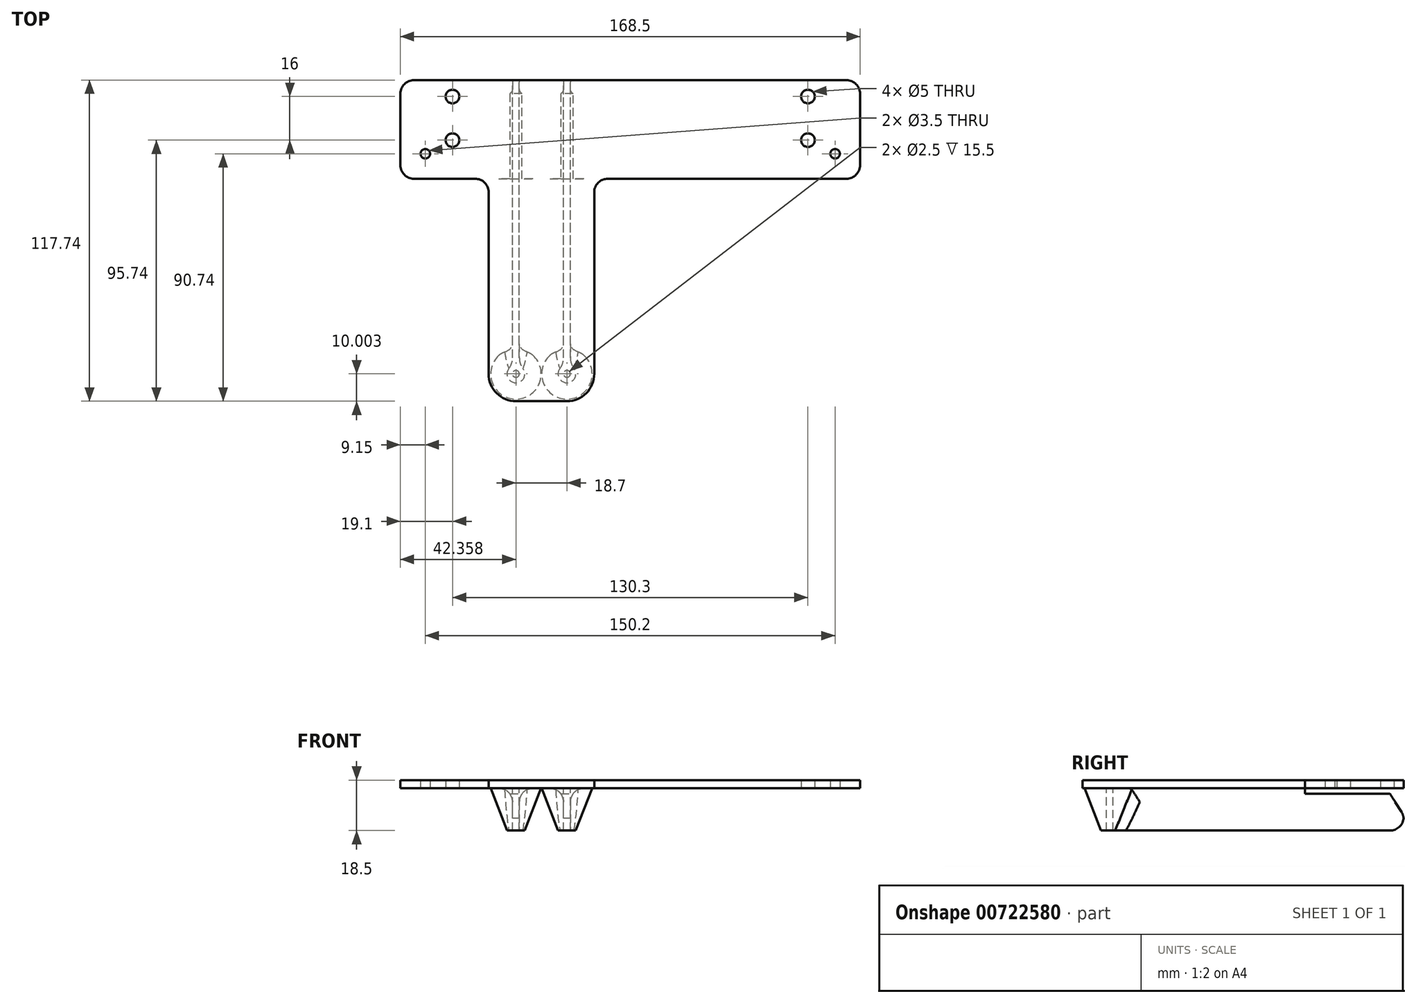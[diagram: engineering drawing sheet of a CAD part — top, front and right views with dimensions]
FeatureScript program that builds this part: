
annotation { "Feature Type Name" : "Feature", "Feature Type Description" : "" }
export const myFeature = defineFeature(function(context is Context, id is Id, definition is map)
    precondition{}
    {
        {
            var Q0;
            Q0=qCreatedBy(makeId("Top.planeOp"),FACE);
            var sketch = newSketch(context, id + "F0", { "sketchPlane" : qUnion([Q0])});
            skLineSegment(sketch, "E0", {"start": v(0, 0) * mm, "end": v(75.1, 0) * mm, "construction": true});
            skCircle(sketch, "E1", {"center": v(75.1, 0) * mm, "radius": 1.75 * mm});
            skCircle(sketch, "E2", {"center": v(75.1, 0) * mm, "radius": 4.15 * mm, "construction": true});
            skLineSegment(sketch, "E3", {"start": v(0, 0) * mm, "end": v(0, 27) * mm, "construction": true});
            skLineSegment(sketch, "E4", {"start": v(0, 5) * mm, "end": v(65.15, 5) * mm, "construction": true});
            skLineSegment(sketch, "E5", {"start": v(65.15, 5) * mm, "end": v(65.15, 21) * mm, "construction": true});
            skCircle(sketch, "E6", {"center": v(65.15, 5) * mm, "radius": 2.5 * mm});
            skCircle(sketch, "E7", {"center": v(65.15, 21) * mm, "radius": 2.5 * mm});
            skCircle(sketch, "E8", {"center": v(-41.9, -80.74) * mm, "radius": 3.25 * mm});
            skCircle(sketch, "E9", {"center": v(-23.2, -80.74) * mm, "radius": 3.25 * mm});
            skCircle(sketch, "E10", {"center": v(-65.15, 5) * mm, "radius": 2.5 * mm});
            skCircle(sketch, "E11", {"center": v(-65.15, 21) * mm, "radius": 2.5 * mm});
            skLineSegment(sketch, "E12", {"start": v(-65.15, 5) * mm, "end": v(0, 5) * mm, "construction": true});
            skCircle(sketch, "E13", {"center": v(-75.1, 0) * mm, "radius": 1.75 * mm});
            skCircle(sketch, "E14", {"center": v(-75.1, 0) * mm, "radius": 4.15 * mm, "construction": true});
            skLineSegment(sketch, "E15", {"start": v(-75.1, 0) * mm, "end": v(0, 0) * mm, "construction": true});
            skLineSegment(sketch, "E16.bottom", {"start": v(-84.25, 27) * mm, "end": v(84.25, 27) * mm});
            skLineSegment(sketch, "E16.top", {"start": v(-84.25, -9.15) * mm, "end": v(84.25, -9.15) * mm});
            skLineSegment(sketch, "E16.left", {"start": v(-84.25, 27) * mm, "end": v(-84.25, -9.15) * mm});
            skLineSegment(sketch, "E16.right", {"start": v(84.25, 27) * mm, "end": v(84.25, -9.15) * mm});
            skArc(sketch, "E17", {"start": v(-51.9, -80.74) * mm, "mid": v(-48.96, -87.8) * mm, "end": v(-41.9, -90.74) * mm});
            skArc(sketch, "E18", {"start": v(-13.2, -80.74) * mm, "mid": v(-16.12, -87.8) * mm, "end": v(-23.2, -90.74) * mm});
            skLineSegment(sketch, "E19", {"start": v(-41.9, -90.74) * mm, "end": v(-23.2, -90.74) * mm});
            skLineSegment(sketch, "E20", {"start": v(-13.2, -80.74) * mm, "end": v(-13.2, -9.15) * mm});
            skLineSegment(sketch, "E21", {"start": v(-51.9, -80.74) * mm, "end": v(-51.9, -9.15) * mm});
            skCircle(sketch, "E22", {"center": v(-23.2, -80.74) * mm, "radius": 1.25 * mm});
            skCircle(sketch, "E23", {"center": v(-41.9, -80.74) * mm, "radius": 1.25 * mm});
            skLineSegment(sketch, "E24", {"start": v(-43.14, -80.74) * mm, "end": v(-43.14, -9.15) * mm});
            skLineSegment(sketch, "E25", {"start": v(-40.64, -80.74) * mm, "end": v(-40.64, -9.15) * mm});
            skLineSegment(sketch, "E26", {"start": v(-24.44, -80.74) * mm, "end": v(-24.44, -9.15) * mm});
            skLineSegment(sketch, "E27", {"start": v(-21.94, -80.74) * mm, "end": v(-21.94, -9.15) * mm});
            skLineSegment(sketch, "E28", {"start": v(-43.14, -9.15) * mm, "end": v(-43.14, 27) * mm});
            skLineSegment(sketch, "E29", {"start": v(-40.64, -9.15) * mm, "end": v(-40.64, 27) * mm});
            skLineSegment(sketch, "E30", {"start": v(-24.44, -9.15) * mm, "end": v(-24.44, 27) * mm});
            skLineSegment(sketch, "E31", {"start": v(-21.94, -9.15) * mm, "end": v(-21.94, 27) * mm});
            skSolve(sketch);
        }
        {
            var Q0;
            Q0=makeQuery(id+"F0.imprint","IMPRINT",FACE,{"disambiguationData":[TD([[makeQuery(id+"F0.imprint","IMPRINT",EDGE,{"derivedFrom":sQuery(id+"F0.wireOp",EDGE,"E8")}),-1.0]])]});
            var Q1;
            Q1=makeQuery(id+"F0.imprint","IMPRINT",FACE,{"disambiguationData":[TD([[makeQuery(id+"F0.imprint","IMPRINT",EDGE,{"derivedFrom":sQuery(id+"F0.wireOp",EDGE,"E8")}),1.0]])]});
            var Q2;
            Q2=makeQuery(id+"F0.imprint","IMPRINT",FACE,{"disambiguationData":[TD([[makeQuery(id+"F0.imprint","IMPRINT",EDGE,{"derivedFrom":sQuery(id+"F0.wireOp",EDGE,"E23")}),1.0]])]});
            var Q3;
            Q3=makeQuery(id+"F0.imprint","IMPRINT",FACE,{"disambiguationData":[TD([[makeQuery(id+"F0.imprint","IMPRINT",EDGE,{"derivedFrom":sQuery(id+"F0.wireOp",EDGE,"E9")}),1.0]])]});
            var Q4;
            Q4=makeQuery(id+"F0.imprint","IMPRINT",FACE,{"disambiguationData":[TD([[makeQuery(id+"F0.imprint","IMPRINT",EDGE,{"derivedFrom":sQuery(id+"F0.wireOp",EDGE,"E22")}),1.0]])]});
            var Q5;
            Q5=makeQuery(id+"F0.imprint","IMPRINT",FACE,{"disambiguationData":[TD([[makeQuery(id+"F0.imprint","IMPRINT",EDGE,{"derivedFrom":sQuery(id+"F0.wireOp",EDGE,"E1")}),-1.0]])]});
            var Q6;
            Q6=makeQuery(id+"F0.imprint","IMPRINT",FACE,{"disambiguationData":[TD([[makeQuery(id+"F0.imprint","IMPRINT",EDGE,{"derivedFrom":sQuery(id+"F0.wireOp",EDGE,"E17")}),1.0]])]});
            var Q7;
            {var subQ0=sQuery(id+"F0.wireOp",EDGE,"E26");var subQ1=sQuery(id+"F0.wireOp",EDGE,"E9");var subQ2=makeQuery(id+"F0.imprint","INTERSECT",VERTEX,{"derivedFrom":[subQ1,subQ0]});Q7=makeQuery(id+"F0.imprint","IMPRINT",FACE,{"disambiguationData":[TD([[makeQuery(id+"F0.imprint","IMPRINT",EDGE,{"disambiguationData":[TD([[subQ2,1.0]])],"derivedFrom":subQ1}),-1.0]])]});}
            var Q8;
            {var subQ0=sQuery(id+"F0.wireOp",EDGE,"E30");Q8=makeQuery(id+"F0.imprint","IMPRINT",FACE,{"disambiguationData":[TD([[makeQuery(id+"F0.imprint","IMPRINT",EDGE,{"derivedFrom":subQ0}),-1.0]])]});}
            var Q9;
            {var subQ0=sQuery(id+"F0.wireOp",EDGE,"E29");Q9=makeQuery(id+"F0.imprint","IMPRINT",FACE,{"disambiguationData":[TD([[makeQuery(id+"F0.imprint","IMPRINT",EDGE,{"derivedFrom":subQ0}),-1.0]])]});}
            var Q10;
            {var subQ0=sQuery(id+"F0.wireOp",EDGE,"E28");Q10=makeQuery(id+"F0.imprint","IMPRINT",FACE,{"disambiguationData":[TD([[makeQuery(id+"F0.imprint","IMPRINT",EDGE,{"derivedFrom":subQ0}),-1.0]])]});}
            var Q11;
            Q11=makeQuery(id+"F0.imprint","IMPRINT",FACE,{"disambiguationData":[TD([[makeQuery(id+"F0.imprint","IMPRINT",EDGE,{"derivedFrom":sQuery(id+"F0.wireOp",EDGE,"E10")}),-1.0]])]});
            extrude(context, id + "F1", {"entities" : qUnion([Q0, Q1, Q2, Q3, Q4, Q5, Q6, Q7, Q8, Q9, Q10, Q11]), "depth" : 3 * mm, "offsetDistance" : 25 * mm});
        }
        {
            var Q0;
            Q0=makeQuery(id+"F0.imprint","IMPRINT",FACE,{"disambiguationData":[TD([[makeQuery(id+"F0.imprint","IMPRINT",EDGE,{"derivedFrom":sQuery(id+"F0.wireOp",EDGE,"E8")}),1.0]])]});
            var Q1;
            Q1=makeQuery(id+"F0.imprint","IMPRINT",FACE,{"disambiguationData":[TD([[makeQuery(id+"F0.imprint","IMPRINT",EDGE,{"derivedFrom":sQuery(id+"F0.wireOp",EDGE,"E9")}),1.0]])]});
            var Q2;
            {var subQ0=sQuery(id+"F0.wireOp",EDGE,"E26");var subQ1=sQuery(id+"F0.wireOp",EDGE,"E9");var subQ2=makeQuery(id+"F0.imprint","INTERSECT",VERTEX,{"derivedFrom":[subQ1,subQ0]});Q2=makeQuery(id+"F0.imprint","IMPRINT",FACE,{"disambiguationData":[TD([[makeQuery(id+"F0.imprint","IMPRINT",EDGE,{"disambiguationData":[TD([[subQ2,1.0]])],"derivedFrom":subQ1}),-1.0]])]});}
            var Q3;
            {var subQ0=sQuery(id+"F0.wireOp",EDGE,"E24");var subQ1=sQuery(id+"F0.wireOp",EDGE,"E8");var subQ2=makeQuery(id+"F0.imprint","INTERSECT",VERTEX,{"derivedFrom":[subQ1,subQ0]});Q3=makeQuery(id+"F0.imprint","IMPRINT",FACE,{"disambiguationData":[TD([[makeQuery(id+"F0.imprint","IMPRINT",EDGE,{"disambiguationData":[TD([[subQ2,1.0]])],"derivedFrom":subQ1}),-1.0]])]});}
            var Q4;
            {var subQ0=sQuery(id+"F0.wireOp",EDGE,"E30");Q4=makeQuery(id+"F0.imprint","IMPRINT",FACE,{"disambiguationData":[TD([[makeQuery(id+"F0.imprint","IMPRINT",EDGE,{"derivedFrom":subQ0}),-1.0]])]});}
            var Q5;
            {var subQ0=sQuery(id+"F0.wireOp",EDGE,"E28");Q5=makeQuery(id+"F0.imprint","IMPRINT",FACE,{"disambiguationData":[TD([[makeQuery(id+"F0.imprint","IMPRINT",EDGE,{"derivedFrom":subQ0}),-1.0]])]});}
            extrude(context, id + "F2", {"entities" : qUnion([Q0, Q1, Q2, Q3, Q4, Q5]), "operationType" : NewBodyOperationType.ADD, "oppositeDirection" : true, "depth" : 15.5 * mm, "offsetDistance" : 25 * mm});
        }
        {
            var Q0;
            {var subQ0=sQuery(id+"F0.wireOp",EDGE,"E30");Q0=makeQuery(id+"F0.imprint","IMPRINT",FACE,{"disambiguationData":[TD([[makeQuery(id+"F0.imprint","IMPRINT",EDGE,{"derivedFrom":subQ0}),-1.0]])]});}
            var Q1;
            {var subQ0=sQuery(id+"F0.wireOp",EDGE,"E28");Q1=makeQuery(id+"F0.imprint","IMPRINT",FACE,{"disambiguationData":[TD([[makeQuery(id+"F0.imprint","IMPRINT",EDGE,{"derivedFrom":subQ0}),-1.0]])]});}
            extrude(context, id + "F3", {"entities" : qUnion([Q0, Q1]), "operationType" : NewBodyOperationType.REMOVE, "oppositeDirection" : true, "depth" : 2 * mm, "offsetDistance" : 25 * mm});
        }
        {
            var Q0;
            Q0=makeQuery(id+"F2.opExtrude","CAP_EDGE",EDGE,{"disambiguationData":[OSD([sQuery(id+"F0.wireOp",EDGE,"E9")])],"isStart":true});
            var Q1;
            Q1=makeQuery(id+"F2.opExtrude","CAP_EDGE",EDGE,{"disambiguationData":[OSD([sQuery(id+"F0.wireOp",EDGE,"E8")])],"isStart":true});
            chamfer(context, id + "F4", {"entities" : qUnion([Q0, Q1]), "chamferType" : ChamferType.TWO_OFFSETS, "width1" : 6 * mm, "oppositeDirection" : false, "width2" : 15.5 * mm, "tangentPropagation" : true});
        }
        {
            var Q0;
            {var subQ0=sQuery(id+"F0.wireOp",EDGE,"E16.bottom");Q0=makeQuery(id+"F3.boolean.opBoolean","COPY",EDGE,{"derivedFrom":makeQuery(id+"F3.opExtrude","CAP_EDGE",EDGE,{"disambiguationData":[OSD([subQ0]),TDD([makeQuery(id+"F0.imprint","IMPRINT",EDGE,{"disambiguationData":[TD([[makeQuery(id+"F0.imprint","INTERSECT",VERTEX,{"derivedFrom":[subQ0,sQuery(id+"F0.wireOp",EDGE,"E30")]}),-1.0]])],"derivedFrom":subQ0})])],"isStart":false})});}
            var Q1;
            {var subQ0=sQuery(id+"F0.wireOp",EDGE,"E16.bottom");Q1=makeQuery(id+"F3.boolean.opBoolean","COPY",EDGE,{"derivedFrom":makeQuery(id+"F3.opExtrude","CAP_EDGE",EDGE,{"disambiguationData":[OSD([subQ0]),TDD([makeQuery(id+"F0.imprint","IMPRINT",EDGE,{"disambiguationData":[TD([[makeQuery(id+"F0.imprint","INTERSECT",VERTEX,{"derivedFrom":[subQ0,sQuery(id+"F0.wireOp",EDGE,"E28")]}),-1.0]])],"derivedFrom":subQ0})])],"isStart":false})});}
            chamfer(context, id + "F5", {"entities" : qUnion([Q0, Q1]), "chamferType" : ChamferType.TWO_OFFSETS, "width1" : 8 * mm, "oppositeDirection" : false, "width2" : 5 * mm, "tangentPropagation" : true});
        }
        {
            var Q0;
            Q0=makeQuery(id+"F1.opExtrude","SWEPT_EDGE",EDGE,{"disambiguationData":[OSD([sQuery(id+"F0.wireOp",EDGE,"E16.top"),sQuery(id+"F0.wireOp",EDGE,"E16.right")])]});
            var Q1;
            Q1=makeQuery(id+"F1.opExtrude","SWEPT_EDGE",EDGE,{"disambiguationData":[OSD([sQuery(id+"F0.wireOp",EDGE,"E16.bottom"),sQuery(id+"F0.wireOp",EDGE,"E16.right")])]});
            var Q2;
            Q2=makeQuery(id+"F1.opExtrude","SWEPT_EDGE",EDGE,{"disambiguationData":[OSD([sQuery(id+"F0.wireOp",EDGE,"E16.top"),sQuery(id+"F0.wireOp",EDGE,"E16.left")])]});
            var Q3;
            Q3=makeQuery(id+"F1.opExtrude","SWEPT_EDGE",EDGE,{"disambiguationData":[OSD([sQuery(id+"F0.wireOp",EDGE,"E16.bottom"),sQuery(id+"F0.wireOp",EDGE,"E16.left")])]});
            var Q4;
            Q4=makeQuery(id+"F1.opExtrude","SWEPT_EDGE",EDGE,{"disambiguationData":[OSD([sQuery(id+"F0.wireOp",EDGE,"E16.top"),sQuery(id+"F0.wireOp",EDGE,"E21")])]});
            var Q5;
            Q5=makeQuery(id+"F1.opExtrude","SWEPT_EDGE",EDGE,{"disambiguationData":[OSD([sQuery(id+"F0.wireOp",EDGE,"E16.top"),sQuery(id+"F0.wireOp",EDGE,"E20")])]});
            var Q6;
            {var subQ0=sQuery(id+"F0.wireOp",EDGE,"E16.bottom");Q6=makeQuery(id+"F2.opExtrude","CAP_EDGE",EDGE,{"disambiguationData":[OSD([subQ0]),TDD([makeQuery(id+"F0.imprint","IMPRINT",EDGE,{"disambiguationData":[TD([[makeQuery(id+"F0.imprint","INTERSECT",VERTEX,{"derivedFrom":[subQ0,sQuery(id+"F0.wireOp",EDGE,"E30")]}),-1.0]])],"derivedFrom":subQ0})])],"isStart":false});}
            var Q7;
            {var subQ0=sQuery(id+"F0.wireOp",EDGE,"E16.bottom");Q7=makeQuery(id+"F2.opExtrude","CAP_EDGE",EDGE,{"disambiguationData":[OSD([subQ0]),TDD([makeQuery(id+"F0.imprint","IMPRINT",EDGE,{"disambiguationData":[TD([[makeQuery(id+"F0.imprint","INTERSECT",VERTEX,{"derivedFrom":[subQ0,sQuery(id+"F0.wireOp",EDGE,"E28")]}),-1.0]])],"derivedFrom":subQ0})])],"isStart":false});}
            var Q8;
            {var subQ1=sQuery(id+"F0.wireOp",EDGE,"E30");var subQ3=sQuery(id+"F0.wireOp",EDGE,"E26");var subQ4=sQuery(id+"F0.wireOp",EDGE,"E16.bottom");var subQ5=makeQuery(id+"F0.imprint","IMPRINT",EDGE,{"disambiguationData":[TD([[makeQuery(id+"F0.imprint","INTERSECT",VERTEX,{"derivedFrom":[subQ4,subQ1]}),-1.0]])],"derivedFrom":subQ4});Q8=makeQuery(id+"F5.opChamfer","BLEND_EDGE",EDGE,{"blendedFrom":[makeQuery(id+"F3.boolean.opBoolean","COPY",EDGE,{"derivedFrom":makeQuery(id+"F3.opExtrude","CAP_EDGE",EDGE,{"disambiguationData":[OSD([subQ4]),TDD([subQ5])],"isStart":false})}),makeQuery(id+"F3.boolean.opBoolean","SPLIT",FACE,{"disambiguationData":[TD([makeQuery(id+"F2.opExtrude","SWEPT_FACE",FACE,{"disambiguationData":[OSD([subQ3,subQ1])]})])],"derivedFrom":makeQuery(id+"F2.boolean.opBoolean","MERGE",FACE,{"derivedFrom":[makeQuery(id+"F1.opExtrude","SWEPT_FACE",FACE,{"disambiguationData":[OSD([subQ4])]}),makeQuery(id+"F2.opExtrude","SWEPT_FACE",FACE,{"disambiguationData":[OSD([subQ4]),TDD([makeQuery(id+"F0.imprint","IMPRINT",EDGE,{"disambiguationData":[TD([[makeQuery(id+"F0.imprint","INTERSECT",VERTEX,{"derivedFrom":[subQ4,sQuery(id+"F0.wireOp",EDGE,"E28")]}),-1.0]])],"derivedFrom":subQ4})])]}),makeQuery(id+"F2.opExtrude","SWEPT_FACE",FACE,{"disambiguationData":[OSD([subQ4]),TDD([subQ5])]})]})})],"blendedInto":[makeQuery(id+"F3.boolean.opBoolean","SPLIT",FACE,{"disambiguationData":[TD([makeQuery(id+"F2.opExtrude","SWEPT_FACE",FACE,{"disambiguationData":[OSD([subQ3,subQ1])]})])],"derivedFrom":makeQuery(id+"F2.boolean.opBoolean","MERGE",FACE,{"derivedFrom":[makeQuery(id+"F1.opExtrude","SWEPT_FACE",FACE,{"disambiguationData":[OSD([subQ4])]}),makeQuery(id+"F2.opExtrude","SWEPT_FACE",FACE,{"disambiguationData":[OSD([subQ4]),TDD([makeQuery(id+"F0.imprint","IMPRINT",EDGE,{"disambiguationData":[TD([[makeQuery(id+"F0.imprint","INTERSECT",VERTEX,{"derivedFrom":[subQ4,sQuery(id+"F0.wireOp",EDGE,"E28")]}),-1.0]])],"derivedFrom":subQ4})])]}),makeQuery(id+"F2.opExtrude","SWEPT_FACE",FACE,{"disambiguationData":[OSD([subQ4]),TDD([subQ5])]})]})})]});}
            var Q9;
            {var subQ1=sQuery(id+"F0.wireOp",EDGE,"E28");var subQ3=sQuery(id+"F0.wireOp",EDGE,"E24");var subQ4=sQuery(id+"F0.wireOp",EDGE,"E16.bottom");var subQ5=makeQuery(id+"F0.imprint","IMPRINT",EDGE,{"disambiguationData":[TD([[makeQuery(id+"F0.imprint","INTERSECT",VERTEX,{"derivedFrom":[subQ4,subQ1]}),-1.0]])],"derivedFrom":subQ4});Q9=makeQuery(id+"F5.opChamfer","BLEND_EDGE",EDGE,{"blendedFrom":[makeQuery(id+"F3.boolean.opBoolean","COPY",EDGE,{"derivedFrom":makeQuery(id+"F3.opExtrude","CAP_EDGE",EDGE,{"disambiguationData":[OSD([subQ4]),TDD([subQ5])],"isStart":false})}),makeQuery(id+"F3.boolean.opBoolean","SPLIT",FACE,{"disambiguationData":[TD([makeQuery(id+"F2.opExtrude","SWEPT_FACE",FACE,{"disambiguationData":[OSD([subQ3,subQ1])]})])],"derivedFrom":makeQuery(id+"F2.boolean.opBoolean","MERGE",FACE,{"derivedFrom":[makeQuery(id+"F1.opExtrude","SWEPT_FACE",FACE,{"disambiguationData":[OSD([subQ4])]}),makeQuery(id+"F2.opExtrude","SWEPT_FACE",FACE,{"disambiguationData":[OSD([subQ4]),TDD([subQ5])]}),makeQuery(id+"F2.opExtrude","SWEPT_FACE",FACE,{"disambiguationData":[OSD([subQ4]),TDD([makeQuery(id+"F0.imprint","IMPRINT",EDGE,{"disambiguationData":[TD([[makeQuery(id+"F0.imprint","INTERSECT",VERTEX,{"derivedFrom":[subQ4,sQuery(id+"F0.wireOp",EDGE,"E30")]}),-1.0]])],"derivedFrom":subQ4})])]})]})})],"blendedInto":[makeQuery(id+"F3.boolean.opBoolean","SPLIT",FACE,{"disambiguationData":[TD([makeQuery(id+"F2.opExtrude","SWEPT_FACE",FACE,{"disambiguationData":[OSD([subQ3,subQ1])]})])],"derivedFrom":makeQuery(id+"F2.boolean.opBoolean","MERGE",FACE,{"derivedFrom":[makeQuery(id+"F1.opExtrude","SWEPT_FACE",FACE,{"disambiguationData":[OSD([subQ4])]}),makeQuery(id+"F2.opExtrude","SWEPT_FACE",FACE,{"disambiguationData":[OSD([subQ4]),TDD([subQ5])]}),makeQuery(id+"F2.opExtrude","SWEPT_FACE",FACE,{"disambiguationData":[OSD([subQ4]),TDD([makeQuery(id+"F0.imprint","IMPRINT",EDGE,{"disambiguationData":[TD([[makeQuery(id+"F0.imprint","INTERSECT",VERTEX,{"derivedFrom":[subQ4,sQuery(id+"F0.wireOp",EDGE,"E30")]}),-1.0]])],"derivedFrom":subQ4})])]})]})})]});}
            var Q10;
            Q10=makeQuery(id+"F2.opExtrude","CAP_EDGE",EDGE,{"disambiguationData":[OSD([sQuery(id+"F0.wireOp",EDGE,"E27"),sQuery(id+"F0.wireOp",EDGE,"E31")])],"isStart":true});
            var Q11;
            Q11=makeQuery(id+"F2.opExtrude","CAP_EDGE",EDGE,{"disambiguationData":[OSD([sQuery(id+"F0.wireOp",EDGE,"E24"),sQuery(id+"F0.wireOp",EDGE,"E28")])],"isStart":true});
            var Q12;
            Q12=makeQuery(id+"F2.opExtrude","CAP_EDGE",EDGE,{"disambiguationData":[OSD([sQuery(id+"F0.wireOp",EDGE,"E25"),sQuery(id+"F0.wireOp",EDGE,"E29")])],"isStart":true});
            var Q13;
            Q13=makeQuery(id+"F2.opExtrude","CAP_EDGE",EDGE,{"disambiguationData":[OSD([sQuery(id+"F0.wireOp",EDGE,"E26"),sQuery(id+"F0.wireOp",EDGE,"E30")])],"isStart":true});
            var Q14;
            Q14=makeQuery(id+"F4.opChamfer","BLEND_EDGE",EDGE,{"blendedFrom":[makeQuery(id+"F2.opExtrude","CAP_EDGE",EDGE,{"disambiguationData":[OSD([sQuery(id+"F0.wireOp",EDGE,"E8")])],"isStart":true}),makeQuery(id+"F2.opExtrude","SWEPT_FACE",FACE,{"disambiguationData":[OSD([sQuery(id+"F0.wireOp",EDGE,"E24"),sQuery(id+"F0.wireOp",EDGE,"E28")])]})],"blendedInto":[makeQuery(id+"F2.opExtrude","SWEPT_FACE",FACE,{"disambiguationData":[OSD([sQuery(id+"F0.wireOp",EDGE,"E24"),sQuery(id+"F0.wireOp",EDGE,"E28")])]})]});
            var Q15;
            Q15=makeQuery(id+"F4.opChamfer","BLEND_EDGE",EDGE,{"blendedFrom":[makeQuery(id+"F2.opExtrude","CAP_EDGE",EDGE,{"disambiguationData":[OSD([sQuery(id+"F0.wireOp",EDGE,"E9")])],"isStart":true}),makeQuery(id+"F2.opExtrude","SWEPT_FACE",FACE,{"disambiguationData":[OSD([sQuery(id+"F0.wireOp",EDGE,"E26"),sQuery(id+"F0.wireOp",EDGE,"E30")])]})],"blendedInto":[makeQuery(id+"F2.opExtrude","SWEPT_FACE",FACE,{"disambiguationData":[OSD([sQuery(id+"F0.wireOp",EDGE,"E26"),sQuery(id+"F0.wireOp",EDGE,"E30")])]})]});
            var Q16;
            Q16=makeQuery(id+"F4.opChamfer","BLEND_EDGE",EDGE,{"blendedFrom":[makeQuery(id+"F2.opExtrude","CAP_EDGE",EDGE,{"disambiguationData":[OSD([sQuery(id+"F0.wireOp",EDGE,"E8")])],"isStart":true}),makeQuery(id+"F2.opExtrude","SWEPT_FACE",FACE,{"disambiguationData":[OSD([sQuery(id+"F0.wireOp",EDGE,"E25"),sQuery(id+"F0.wireOp",EDGE,"E29")])]})],"blendedInto":[makeQuery(id+"F2.opExtrude","SWEPT_FACE",FACE,{"disambiguationData":[OSD([sQuery(id+"F0.wireOp",EDGE,"E25"),sQuery(id+"F0.wireOp",EDGE,"E29")])]})]});
            var Q17;
            Q17=makeQuery(id+"F4.opChamfer","BLEND_EDGE",EDGE,{"blendedFrom":[makeQuery(id+"F2.opExtrude","CAP_EDGE",EDGE,{"disambiguationData":[OSD([sQuery(id+"F0.wireOp",EDGE,"E9")])],"isStart":true}),makeQuery(id+"F2.opExtrude","SWEPT_FACE",FACE,{"disambiguationData":[OSD([sQuery(id+"F0.wireOp",EDGE,"E27"),sQuery(id+"F0.wireOp",EDGE,"E31")])]})],"blendedInto":[makeQuery(id+"F2.opExtrude","SWEPT_FACE",FACE,{"disambiguationData":[OSD([sQuery(id+"F0.wireOp",EDGE,"E27"),sQuery(id+"F0.wireOp",EDGE,"E31")])]})]});
            fillet(context, id + "F6", {"entities" : qUnion([Q0, Q1, Q2, Q3, Q4, Q5, Q6, Q7, Q8, Q9, Q10, Q11, Q12, Q13, Q14, Q15, Q16, Q17]), "radius" : 5 * mm, "tangentPropagation" : true, "allowEdgeOverflow" : false});
        }
    });
